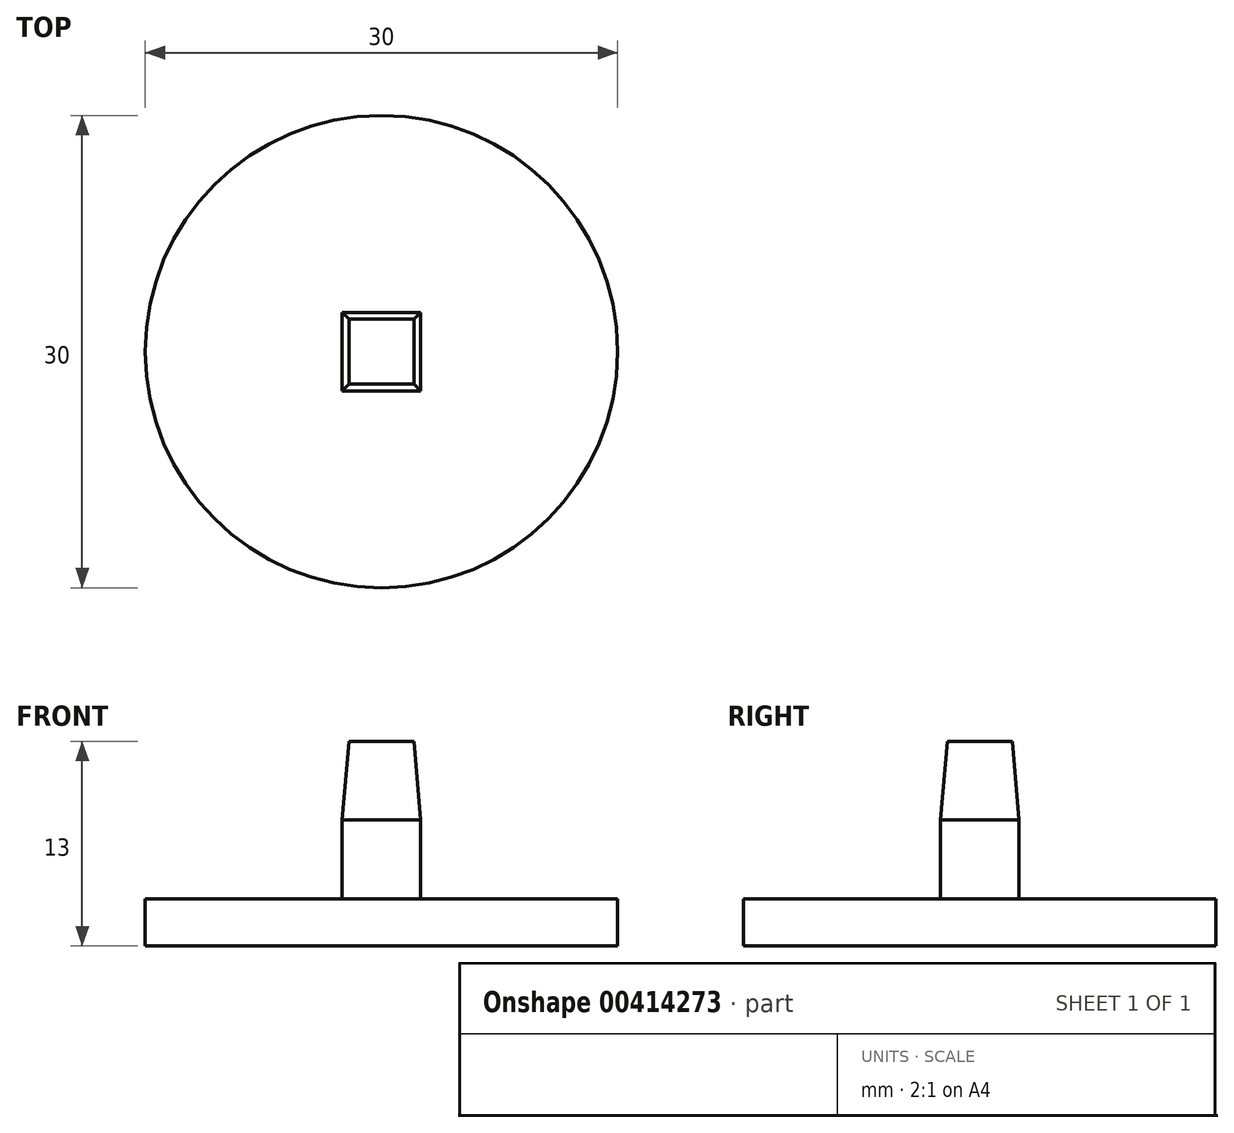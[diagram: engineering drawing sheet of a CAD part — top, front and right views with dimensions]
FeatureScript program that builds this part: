
annotation { "Feature Type Name" : "Feature", "Feature Type Description" : "" }
export const myFeature = defineFeature(function(context is Context, id is Id, definition is map)
    precondition{}
    {
        {
            var Q0;
            Q0=qCreatedBy(makeId("Top.planeOp"),FACE);
            var sketch = newSketch(context, id + "F0", { "sketchPlane" : qUnion([Q0])});
            skCircle(sketch, "E0", {"center": v(0, 0) * mm, "radius": 15 * mm});
            skLineSegment(sketch, "E1.bottom", {"start": v(2.5, -2.5) * mm, "end": v(-2.5, -2.5) * mm});
            skLineSegment(sketch, "E1.top", {"start": v(2.5, 2.5) * mm, "end": v(-2.5, 2.5) * mm});
            skLineSegment(sketch, "E1.left", {"start": v(2.5, -2.5) * mm, "end": v(2.5, 2.5) * mm});
            skLineSegment(sketch, "E1.right", {"start": v(-2.5, -2.5) * mm, "end": v(-2.5, 2.5) * mm});
            skSolve(sketch);
        }
        {
            var Q0;
            Q0 = qSketchRegion(id + "F0", true);
            extrude(context, id + "F1", {"entities" : qUnion([Q0]), "depth" : 3 * mm});
        }
        {
            var Q0;
            Q0=makeQuery(id+"F0.imprint","IMPRINT",FACE,{"disambiguationData":[TD([[makeQuery(id+"F0.imprint","IMPRINT",EDGE,{"derivedFrom":sQuery(id+"F0.wireOp",EDGE,"E1.bottom")}),-1.0]])]});
            extrude(context, id + "F2", {"entities" : qUnion([Q0]), "operationType" : NewBodyOperationType.ADD, "depth" : 8 * mm});
        }
        {
            var Q0;
            Q0=makeQuery(id+"F2.opExtrude","CAP_FACE",FACE,{"disambiguationData":[OSD([sQuery(id+"F0.wireOp",EDGE,"E1.bottom"),sQuery(id+"F0.wireOp",EDGE,"E1.top"),sQuery(id+"F0.wireOp",EDGE,"E1.left"),sQuery(id+"F0.wireOp",EDGE,"E1.right")])],"isStart":false});
            extrude(context, id + "F3", {"entities" : qUnion([Q0]), "operationType" : NewBodyOperationType.ADD, "depth" : 5 * mm, "hasDraft" : true, "draftAngle" : 5 * degree, "draftPullDirection" : true});
        }
    });
